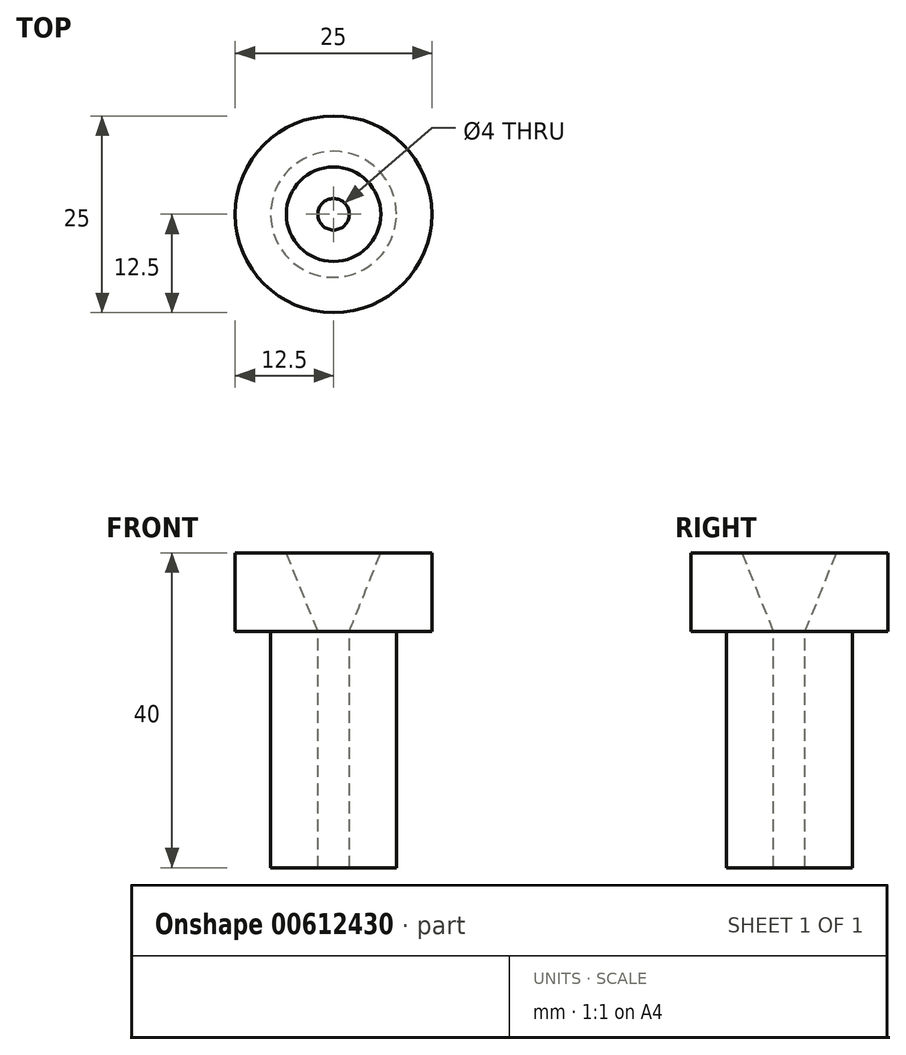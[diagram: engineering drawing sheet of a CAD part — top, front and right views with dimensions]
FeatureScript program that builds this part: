
annotation { "Feature Type Name" : "Feature", "Feature Type Description" : "" }
export const myFeature = defineFeature(function(context is Context, id is Id, definition is map)
    precondition{}
    {
        {
            var Q0;
            Q0=qCreatedBy(makeId("Top.planeOp"),FACE);
            var sketch = newSketch(context, id + "F0", { "sketchPlane" : qUnion([Q0])});
            skCircle(sketch, "E0", {"center": v(0, 0) * mm, "radius": 8 * mm});
            skSolve(sketch);
        }
        {
            var Q0;
            Q0=makeQuery(id+"F0.imprint","IMPRINT",FACE,{"disambiguationData":[TD([[makeQuery(id+"F0.imprint","IMPRINT",EDGE,{"derivedFrom":sQuery(id+"F0.wireOp",EDGE,"E0")}),1.0]])]});
            extrude(context, id + "F1", {"entities" : qUnion([Q0]), "oppositeDirection" : true, "depth" : 30 * mm, "offsetDistance" : 25 * mm});
        }
        {
            var Q0;
            Q0=makeQuery(id+"F1.opExtrude","CAP_FACE",FACE,{"disambiguationData":[OSD([sQuery(id+"F0.wireOp",EDGE,"E0")])],"isStart":true});
            var sketch = newSketch(context, id + "F2", { "sketchPlane" : qUnion([Q0])});
            skCircle(sketch, "E1", {"center": v(0, 0) * mm, "radius": 2 * mm});
            skSolve(sketch);
        }
        {
            var Q0;
            Q0 = qSketchRegion(id + "F2", true);
            extrude(context, id + "F3", {"entities" : qUnion([Q0]), "operationType" : NewBodyOperationType.REMOVE, "oppositeDirection" : true, "depth" : 30 * mm, "offsetDistance" : 25 * mm});
        }
        {
            var Q0;
            Q0=makeQuery(id+"F1.opExtrude","CAP_FACE",FACE,{"disambiguationData":[OSD([sQuery(id+"F0.wireOp",EDGE,"E0")])],"isStart":true});
            var sketch = newSketch(context, id + "F4", { "sketchPlane" : qUnion([Q0])});
            skCircle(sketch, "E2", {"center": v(0, 0) * mm, "radius": 12.5 * mm});
            skSolve(sketch);
        }
        {
            var Q0;
            Q0=makeQuery(id+"F4.imprint","IMPRINT",FACE,{"disambiguationData":[TD([[makeQuery(id+"F4.imprint","IMPRINT",EDGE,{"derivedFrom":sQuery(id+"F4.wireOp",EDGE,"E2")}),1.0]])]});
            var Q1;
            Q1=makeQuery(id+"F4.imprint","IMPRINT",FACE,{"disambiguationData":[TD([[makeQuery(id+"F4.imprint","IMPRINT",EDGE,{"derivedFrom":makeQuery(id+"F1.opExtrude","CAP_EDGE",EDGE,{"disambiguationData":[OSD([sQuery(id+"F0.wireOp",EDGE,"E0")])],"isStart":true})}),1.0]])]});
            var Q2;
            Q2=sQuery(id+"F4.wireOp",EDGE,"E2");
            extrude(context, id + "F5", {"entities" : qUnion([Q0, Q1]), "surfaceEntities" : qUnion([Q2]), "depth" : 10 * mm, "offsetDistance" : 25 * mm});
        }
        {
            var Q0;
            Q0=makeQuery(id+"F5.opExtrude","CAP_EDGE",EDGE,{"disambiguationData":[OSD([sQuery(id+"F2.wireOp",EDGE,"E1")])],"isStart":false});
            chamfer(context, id + "F6", {"entities" : qUnion([Q0]), "chamferType" : ChamferType.TWO_OFFSETS, "width1" : 4 * mm, "oppositeDirection" : true, "width2" : 10 * mm, "tangentPropagation" : true});
        }
    });
